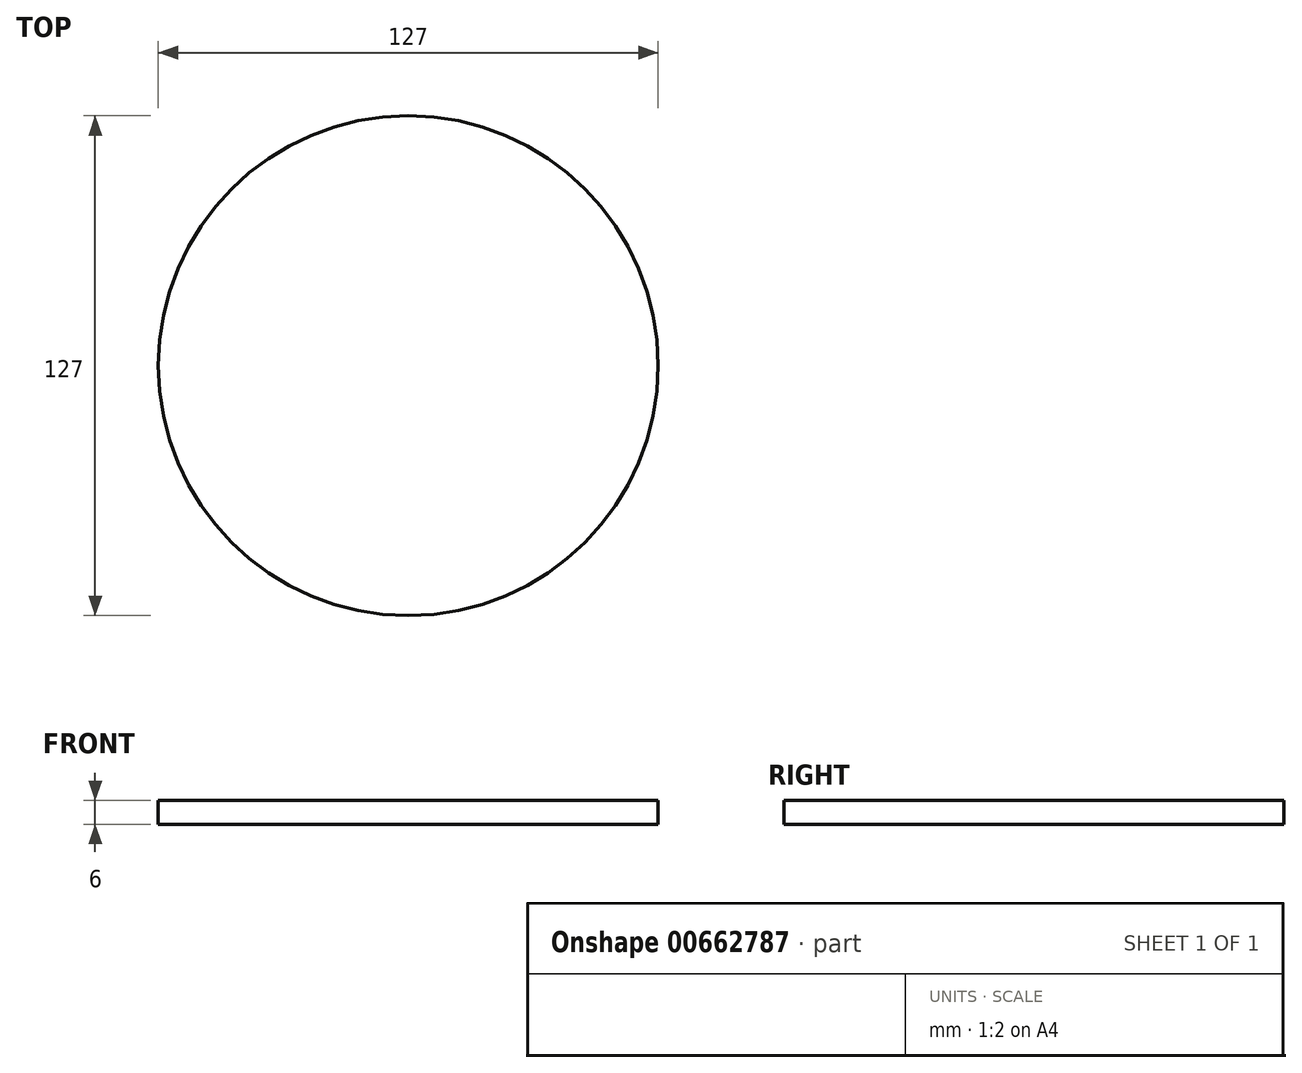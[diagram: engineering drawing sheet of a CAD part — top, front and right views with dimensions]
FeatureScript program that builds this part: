
annotation { "Feature Type Name" : "Feature", "Feature Type Description" : "" }
export const myFeature = defineFeature(function(context is Context, id is Id, definition is map)
    precondition{}
    {
        {
            var Q0;
            Q0=qCreatedBy(makeId("Front.planeOp"),FACE);
            var sketch = newSketch(context, id + "F0", { "sketchPlane" : qUnion([Q0])});
            skLineSegment(sketch, "E0.bottom", {"start": v(0, 0) * mm, "end": v(-63.5, 0) * mm});
            skLineSegment(sketch, "E0.top", {"start": v(0, 6) * mm, "end": v(-63.5, 6) * mm});
            skLineSegment(sketch, "E0.left", {"start": v(0, 0) * mm, "end": v(0, 6) * mm});
            skLineSegment(sketch, "E0.right", {"start": v(-63.5, 0) * mm, "end": v(-63.5, 6) * mm});
            skSolve(sketch);
        }
        {
            var Q0;
            Q0 = qSketchRegion(id + "F0", true);
            var Q1;
            Q1=sQuery(id+"F0.wireOp",EDGE,"E0.left");
            revolve(context, id + "F1", {"entities" : qUnion([Q0]), "axis" : qUnion([Q1]), "revolveType" : RevolveType.FULL});
        }
    });
